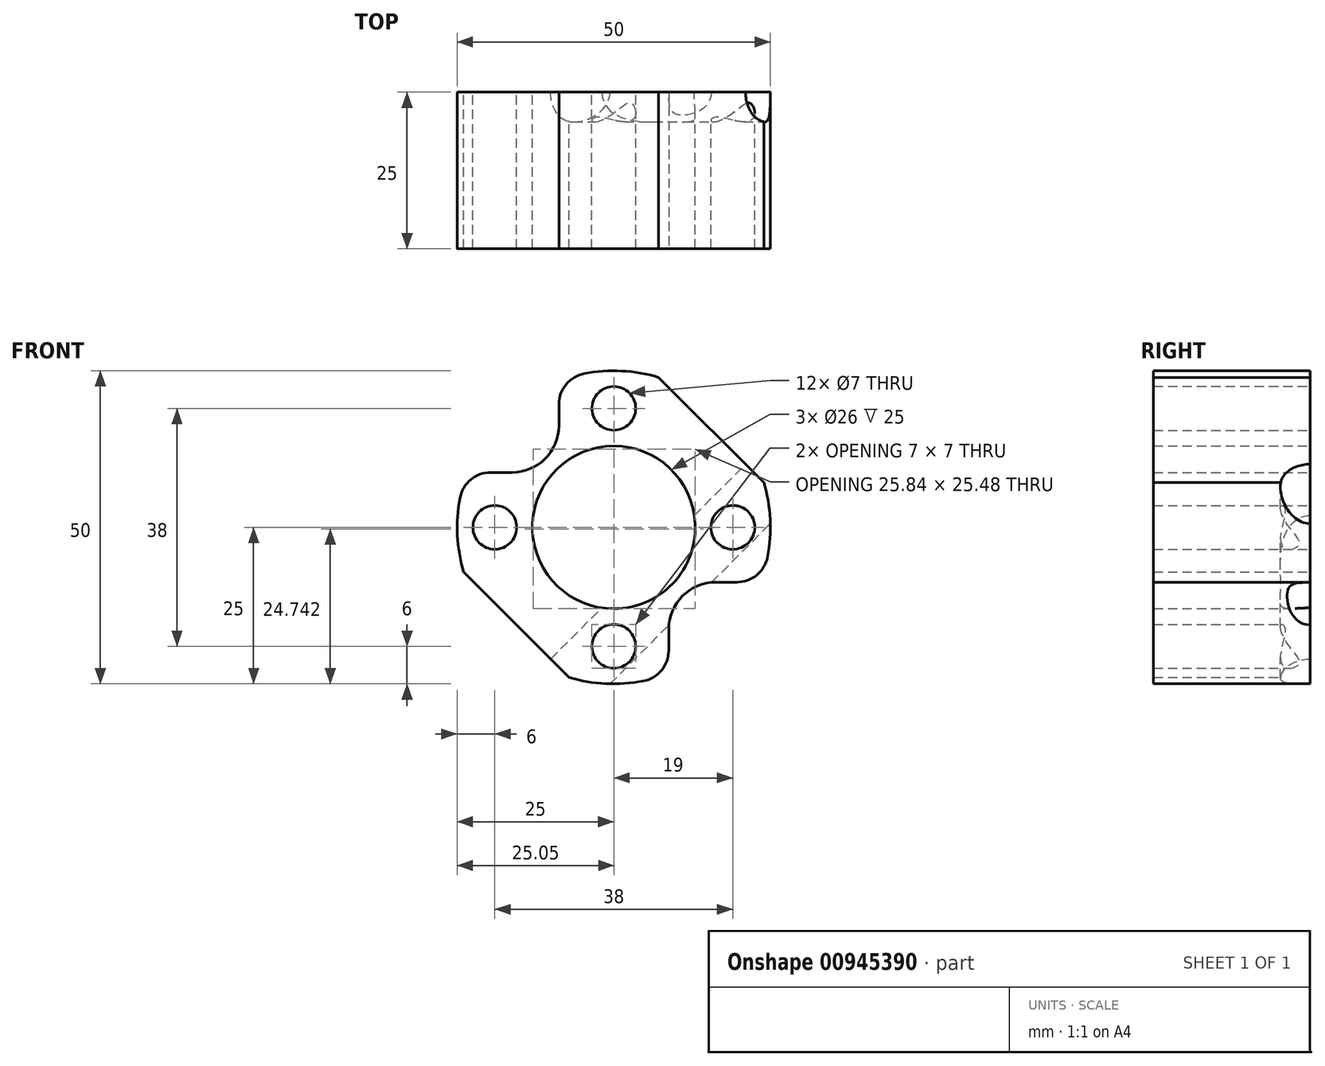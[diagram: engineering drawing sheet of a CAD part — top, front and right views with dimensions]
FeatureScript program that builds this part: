
annotation { "Feature Type Name" : "Feature", "Feature Type Description" : "" }
export const myFeature = defineFeature(function(context is Context, id is Id, definition is map)
    precondition{}
    {
        {
            var Q0;
            Q0=qCreatedBy(makeId("Front.planeOp"),FACE);
            var sketch = newSketch(context, id + "F0", { "sketchPlane" : qUnion([Q0])});
            skCircle(sketch, "E0", {"center": v(0, 0) * mm, "radius": 25 * mm});
            skCircle(sketch, "E1", {"center": v(0, 0) * mm, "radius": 13.5 * mm, "construction": true});
            skCircle(sketch, "E2", {"center": v(0, 19) * mm, "radius": 3.5 * mm});
            skCircle(sketch, "E3.MirrorC", {"center": v(0, -19) * mm, "radius": 3.5 * mm});
            skCircle(sketch, "E4", {"center": v(19, 0) * mm, "radius": 3.5 * mm});
            skCircle(sketch, "E5.MirrorC", {"center": v(-19, 0) * mm, "radius": 3.5 * mm});
            skSolve(sketch);
        }
        {
            var Q0;
            Q0=qSketchRegion(id+"F0",true);
            extrude(context, id + "F1", {"entities" : qUnion([Q0]), "depth" : 25 * mm, "offsetDistance" : 25 * mm});
        }
        {
            var Q0;
            Q0=qCreatedBy(makeId("Front.planeOp"),FACE);
            var sketch = newSketch(context, id + "F2", { "sketchPlane" : qUnion([Q0])});
            skPoint(sketch, "E6.middle", {"position": v(0, 0) * mm});
            skCircle(sketch, "E7", {"center": v(-16.26, 16.26) * mm, "radius": 2.5 * mm, "construction": true});
            skLineSegment(sketch, "E8", {"start": v(0, 0) * mm, "end": v(-39.56, 39.56) * mm, "construction": true});
            skLineSegment(sketch, "E9.bottom", {"start": v(-16.26, 8.76) * mm, "end": v(-23.76, 8.76) * mm});
            skLineSegment(sketch, "E9.top", {"start": v(-8.76, 23.76) * mm, "end": v(-23.76, 23.76) * mm});
            skLineSegment(sketch, "E9.left", {"start": v(-8.76, 16.26) * mm, "end": v(-8.76, 23.76) * mm});
            skLineSegment(sketch, "E9.right", {"start": v(-23.76, 8.76) * mm, "end": v(-23.76, 23.76) * mm});
            skPoint(sketch, "E10.visualSharp", {"position": v(-8.76, 8.76) * mm});
            skArc(sketch, "E10.filletArc", {"start": v(-16.26, 8.76) * mm, "mid": v(-10.96, 10.96) * mm, "end": v(-8.76, 16.26) * mm});
            skLineSegment(sketch, "E11.MirrorCS", {"start": v(8.76, 16.26) * mm, "end": v(8.76, 23.76) * mm, "construction": true});
            skArc(sketch, "E12.MirrorCS", {"start": v(16.26, 8.76) * mm, "mid": v(10.96, 10.96) * mm, "end": v(8.76, 16.26) * mm, "construction": true});
            skLineSegment(sketch, "E13.MirrorCS", {"start": v(16.26, 8.76) * mm, "end": v(23.76, 8.76) * mm, "construction": true});
            skLineSegment(sketch, "E14.MirrorCS", {"start": v(23.76, 8.76) * mm, "end": v(23.76, 23.76) * mm, "construction": true});
            skLineSegment(sketch, "E15.MirrorCS", {"start": v(8.76, 23.76) * mm, "end": v(23.76, 23.76) * mm, "construction": true});
            skLineSegment(sketch, "E16.MirrorCS", {"start": v(-16.26, -8.76) * mm, "end": v(-23.76, -8.76) * mm, "construction": true});
            skLineSegment(sketch, "E17.MirrorCS", {"start": v(-23.76, -8.76) * mm, "end": v(-23.76, -23.76) * mm, "construction": true});
            skLineSegment(sketch, "E18.MirrorCS", {"start": v(-8.76, -23.76) * mm, "end": v(-23.76, -23.76) * mm, "construction": true});
            skLineSegment(sketch, "E19.MirrorCS", {"start": v(-8.76, -16.26) * mm, "end": v(-8.76, -23.76) * mm, "construction": true});
            skArc(sketch, "E20.MirrorCS", {"start": v(-16.26, -8.76) * mm, "mid": v(-10.96, -10.96) * mm, "end": v(-8.76, -16.26) * mm, "construction": true});
            skLineSegment(sketch, "E21.MirrorCS", {"start": v(8.76, -16.26) * mm, "end": v(8.76, -23.76) * mm});
            skArc(sketch, "E22.MirrorCS", {"start": v(16.26, -8.76) * mm, "mid": v(10.96, -10.96) * mm, "end": v(8.76, -16.26) * mm});
            skLineSegment(sketch, "E23.MirrorCS", {"start": v(16.26, -8.76) * mm, "end": v(23.76, -8.76) * mm});
            skLineSegment(sketch, "E24.MirrorCS", {"start": v(23.76, -8.76) * mm, "end": v(23.76, -23.76) * mm});
            skLineSegment(sketch, "E25.MirrorCS", {"start": v(8.76, -23.76) * mm, "end": v(23.76, -23.76) * mm});
            skLineSegment(sketch, "E26", {"start": v(0, 0) * mm, "end": v(42.56, 42.56) * mm, "construction": true});
            skLineSegment(sketch, "E27", {"start": v(29.7, 1.41) * mm, "end": v(1.41, 29.7) * mm});
            skLineSegment(sketch, "E28", {"start": v(1.41, 29.7) * mm, "end": v(33.37, 61.66) * mm});
            skLineSegment(sketch, "E29", {"start": v(33.37, 61.66) * mm, "end": v(61.4, 33.64) * mm});
            skLineSegment(sketch, "E30", {"start": v(61.4, 33.64) * mm, "end": v(29.7, 1.41) * mm});
            skLineSegment(sketch, "E31.MirrorCS", {"start": v(-29.7, -1.41) * mm, "end": v(-61.66, -33.37) * mm});
            skLineSegment(sketch, "E32.MirrorCS", {"start": v(-1.41, -29.7) * mm, "end": v(-29.7, -1.41) * mm});
            skLineSegment(sketch, "E33.MirrorCS", {"start": v(-33.64, -61.4) * mm, "end": v(-1.41, -29.7) * mm});
            skLineSegment(sketch, "E34.MirrorCS", {"start": v(-61.66, -33.37) * mm, "end": v(-33.64, -61.4) * mm});
            skSolve(sketch);
        }
        {
            var Q0;
            Q0=makeQuery(id+"F2.imprint","IMPRINT",FACE,{"disambiguationData":[TD([[makeQuery(id+"F2.imprint","IMPRINT",EDGE,{"derivedFrom":sQuery(id+"F2.wireOp",EDGE,"E9.bottom")}),-1.0]])]});
            var Q1;
            Q1=makeQuery(id+"F2.imprint","IMPRINT",FACE,{"disambiguationData":[TD([[makeQuery(id+"F2.imprint","IMPRINT",EDGE,{"derivedFrom":sQuery(id+"F2.wireOp",EDGE,"E11.MirrorCS")}),-1.0]])]});
            var Q2;
            Q2=makeQuery(id+"F2.imprint","IMPRINT",FACE,{"disambiguationData":[TD([[makeQuery(id+"F2.imprint","IMPRINT",EDGE,{"derivedFrom":sQuery(id+"F2.wireOp",EDGE,"E16.MirrorCS")}),1.0]])]});
            var Q3;
            Q3=makeQuery(id+"F2.imprint","IMPRINT",FACE,{"disambiguationData":[TD([[makeQuery(id+"F2.imprint","IMPRINT",EDGE,{"derivedFrom":sQuery(id+"F2.wireOp",EDGE,"E21.MirrorCS")}),1.0]])]});
            var Q4;
            Q4=makeQuery(id+"F2.imprint","IMPRINT",FACE,{"disambiguationData":[TD([[makeQuery(id+"F2.imprint","IMPRINT",EDGE,{"derivedFrom":sQuery(id+"F2.wireOp",EDGE,"E27")}),-1.0]])]});
            var Q5;
            Q5=makeQuery(id+"F2.imprint","IMPRINT",FACE,{"disambiguationData":[TD([[makeQuery(id+"F2.imprint","IMPRINT",EDGE,{"derivedFrom":sQuery(id+"F2.wireOp",EDGE,"E31.MirrorCS")}),1.0]])]});
            extrude(context, id + "F3", {"entities" : qUnion([Q0, Q1, Q2, Q3, Q4, Q5]), "operationType" : NewBodyOperationType.REMOVE, "endBound" : BoundingType.THROUGH_ALL, "depth" : 25 * mm, "offsetDistance" : 25 * mm});
        }
        {
            var Q0;
            Q0=makeQuery(id+"F3.boolean.opBoolean","INTERSECT",EDGE,{"derivedFrom":[makeQuery(id+"F1.opExtrude","SWEPT_FACE",FACE,{"disambiguationData":[OSD([sQuery(id+"F0.wireOp",EDGE,"E0")])]}),makeQuery(id+"F3.opExtrude","SWEPT_FACE",FACE,{"disambiguationData":[OSD([sQuery(id+"F2.wireOp",EDGE,"E11.MirrorCS")])]})]});
            var Q1;
            Q1=makeQuery(id+"F3.boolean.opBoolean","INTERSECT",EDGE,{"derivedFrom":[makeQuery(id+"F1.opExtrude","SWEPT_FACE",FACE,{"disambiguationData":[OSD([sQuery(id+"F0.wireOp",EDGE,"E0")])]}),makeQuery(id+"F3.opExtrude","SWEPT_FACE",FACE,{"disambiguationData":[OSD([sQuery(id+"F2.wireOp",EDGE,"E9.left")])]})]});
            var Q2;
            Q2=makeQuery(id+"F3.boolean.opBoolean","INTERSECT",EDGE,{"derivedFrom":[makeQuery(id+"F1.opExtrude","SWEPT_FACE",FACE,{"disambiguationData":[OSD([sQuery(id+"F0.wireOp",EDGE,"E0")])]}),makeQuery(id+"F3.opExtrude","SWEPT_FACE",FACE,{"disambiguationData":[OSD([sQuery(id+"F2.wireOp",EDGE,"E9.bottom")])]})]});
            var Q3;
            Q3=makeQuery(id+"F3.boolean.opBoolean","INTERSECT",EDGE,{"derivedFrom":[makeQuery(id+"F1.opExtrude","SWEPT_FACE",FACE,{"disambiguationData":[OSD([sQuery(id+"F0.wireOp",EDGE,"E0")])]}),makeQuery(id+"F3.opExtrude","SWEPT_FACE",FACE,{"disambiguationData":[OSD([sQuery(id+"F2.wireOp",EDGE,"E16.MirrorCS")])]})]});
            var Q4;
            Q4=makeQuery(id+"F3.boolean.opBoolean","INTERSECT",EDGE,{"derivedFrom":[makeQuery(id+"F1.opExtrude","SWEPT_FACE",FACE,{"disambiguationData":[OSD([sQuery(id+"F0.wireOp",EDGE,"E0")])]}),makeQuery(id+"F3.opExtrude","SWEPT_FACE",FACE,{"disambiguationData":[OSD([sQuery(id+"F2.wireOp",EDGE,"E19.MirrorCS")])]})]});
            var Q5;
            Q5=makeQuery(id+"F3.boolean.opBoolean","INTERSECT",EDGE,{"derivedFrom":[makeQuery(id+"F1.opExtrude","SWEPT_FACE",FACE,{"disambiguationData":[OSD([sQuery(id+"F0.wireOp",EDGE,"E0")])]}),makeQuery(id+"F3.opExtrude","SWEPT_FACE",FACE,{"disambiguationData":[OSD([sQuery(id+"F2.wireOp",EDGE,"E21.MirrorCS")])]})]});
            var Q6;
            Q6=makeQuery(id+"F3.boolean.opBoolean","INTERSECT",EDGE,{"derivedFrom":[makeQuery(id+"F1.opExtrude","SWEPT_FACE",FACE,{"disambiguationData":[OSD([sQuery(id+"F0.wireOp",EDGE,"E0")])]}),makeQuery(id+"F3.opExtrude","SWEPT_FACE",FACE,{"disambiguationData":[OSD([sQuery(id+"F2.wireOp",EDGE,"E23.MirrorCS")])]})]});
            var Q7;
            Q7=makeQuery(id+"F3.boolean.opBoolean","INTERSECT",EDGE,{"derivedFrom":[makeQuery(id+"F1.opExtrude","SWEPT_FACE",FACE,{"disambiguationData":[OSD([sQuery(id+"F0.wireOp",EDGE,"E0")])]}),makeQuery(id+"F3.opExtrude","SWEPT_FACE",FACE,{"disambiguationData":[OSD([sQuery(id+"F2.wireOp",EDGE,"E13.MirrorCS")])]})]});
            fillet(context, id + "F4", {"entities" : qUnion([Q0, Q1, Q2, Q3, Q4, Q5, Q6, Q7]), "radius" : 5 * mm, "tangentPropagation" : true, "allowEdgeOverflow" : false});
        }
        {
            var Q0;
            Q0=qCreatedBy(makeId("Front.planeOp"),FACE);
            var sketch = newSketch(context, id + "F5", { "sketchPlane" : qUnion([Q0])});
            skCircle(sketch, "E35", {"center": v(0, 0) * mm, "radius": 13 * mm});
            skSolve(sketch);
        }
        {
            var Q0;
            Q0=qSketchRegion(id+"F5",true);
            extrude(context, id + "F6", {"entities" : qUnion([Q0]), "operationType" : NewBodyOperationType.REMOVE, "endBound" : BoundingType.THROUGH_ALL, "depth" : 25 * mm, "offsetDistance" : 25 * mm});
        }
        {
            var Q0;
            Q0=makeQuery(id+"F3.boolean.opBoolean","COPY",FACE,{"derivedFrom":makeQuery(id+"F3.opExtrude","SWEPT_FACE",FACE,{"disambiguationData":[OSD([sQuery(id+"F2.wireOp",EDGE,"E27")])]})});
            var sketch = newSketch(context, id + "F7", { "sketchPlane" : qUnion([Q0])});
            skCircle(sketch, "E36", {"center": v(0, -12.5) * mm, "radius": 4.75 * mm});
            skPoint(sketch, "E36.centerSnap0", {"position": v(-10.54, -12.5) * mm});
            skSolve(sketch);
        }
        {
            var Q0;
            Q0 = qSketchRegion(id + "F7", true);
            extrude(context, id + "F8", {"entities" : qUnion([Q0]), "operationType" : NewBodyOperationType.REMOVE, "endBound" : BoundingType.THROUGH_ALL, "oppositeDirection" : true, "depth" : 25 * mm, "offsetDistance" : 25 * mm});
        }
    });
